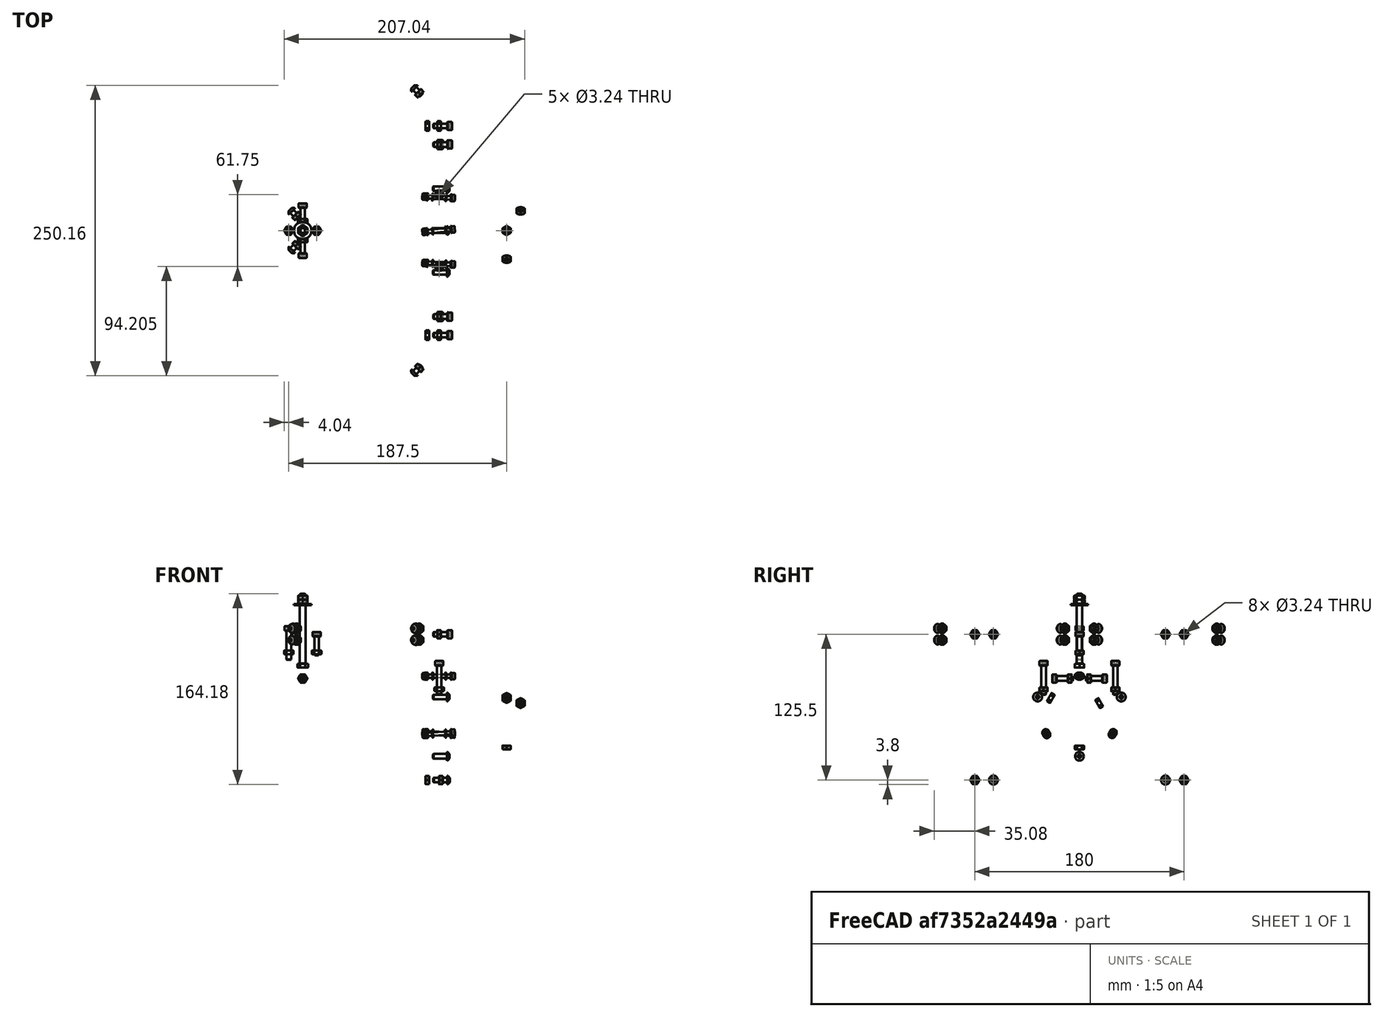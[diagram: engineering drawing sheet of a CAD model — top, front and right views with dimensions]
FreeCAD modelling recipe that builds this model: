
FCSTD DOCUMENT  (FreeCAD 0.19R24276 (Git))
Label: v5.6_Secondary
License: All rights reserved
LicenseURL: http://en.wikipedia.org/wiki/All_rights_reserved
objects: Part::FeaturePython×70, App::Link×28, App::DocumentObjectGroup×2, PartDesign::CoordinateSystem×1, App::FeaturePython×1, App::Part×1
note: 71 computed .brp shape members not serialized (recipe doc carries the construction recipe); baked Part::Feature solids carry a one-line shape summary decoded from their .brp
EXTERNAL_REF file=v5.6_Master.FCStd obj=Local_CS140
EXTERNAL_REF file=v5.6_Master.FCStd obj=Body022002
EXTERNAL_REF file=v5.6_Master.FCStd obj=Local_CS226
EXTERNAL_REF file=v5.6_Master.FCStd obj=Local_CS227
EXTERNAL_REF file=v5.6_Master.FCStd obj=Body001
EXTERNAL_REF file=v5.6_Master.FCStd obj=Local_CS003
EXTERNAL_REF file=v5.6_Master.FCStd obj=Local_CS124
EXTERNAL_REF file=v5.6_Master.FCStd obj=Body022003
EXTERNAL_REF file=v5.6_Master.FCStd obj=Local_CS062
EXTERNAL_REF file=v5.6_Master.FCStd obj=Local_CS125
EXTERNAL_REF file=v5.6_Master.FCStd obj=Body009
EXTERNAL_REF file=v5.6_Master.FCStd obj=Local_CS142
EXTERNAL_REF file=v5.6_Master.FCStd obj=Local_CS147
EXTERNAL_REF file=v5.6_Master.FCStd obj=Body011
EXTERNAL_REF file=v5.6_Master.FCStd obj=Local_CS143
EXTERNAL_REF file=v5.6_Master.FCStd obj=Local_CS146
EXTERNAL_REF file=v5.6_Master.FCStd obj=Local_CS155
EXTERNAL_REF file=v5.6_Master.FCStd obj=Local_CS181
EXTERNAL_REF file=v5.6_Master.FCStd obj=Body022005
EXTERNAL_REF file=v5.6_Master.FCStd obj=Local_CS137
EXTERNAL_REF file=v5.6_Master.FCStd obj=Local_CS201
EXTERNAL_REF file=v5.6_Master.FCStd obj=Body022004
EXTERNAL_REF file=v5.6_Master.FCStd obj=Local_CS132
EXTERNAL_REF file=v5.6_Master.FCStd obj=Local_CS134
EXTERNAL_REF file=v5.6_Master.FCStd obj=Body008
EXTERNAL_REF file=v5.6_Master.FCStd obj=Local_CS047
EXTERNAL_REF file=v5.6_Master.FCStd obj=Local_CS130
EXTERNAL_REF file=v5.6_Master.FCStd obj=Body007
EXTERNAL_REF file=v5.6_Master.FCStd obj=Local_CS046
EXTERNAL_REF file=v5.6_Master.FCStd obj=Local_CS193
EXTERNAL_REF file=v5.6_Master.FCStd obj=Body022012
EXTERNAL_REF file=v5.6_Master.FCStd obj=Local_CS036
EXTERNAL_REF file=v5.6_Master.FCStd obj=Local_CS035
EXTERNAL_REF file=v5.6_Master.FCStd obj=Local_CS045
EXTERNAL_REF file=v5.6_Master.FCStd obj=Local_CS034
EXTERNAL_REF file=v5.6_Master.FCStd obj=Local_CS033
EXTERNAL_REF file=v5.6_Master.FCStd obj=Local_CS194
EXTERNAL_REF file=v5.6_Master.FCStd obj=Local_CS123
EXTERNAL_REF file=v5.6_Master.FCStd obj=Local_CS126
EXTERNAL_REF file=v5.6_Master.FCStd obj=Local_CS127
EXTERNAL_REF file=v5.6_Master.FCStd obj=Local_CS060
EXTERNAL_REF file=v5.6_Master.FCStd obj=Local_CS136
EXTERNAL_REF file=v5.6_Master.FCStd obj=Local_CS055
EXTERNAL_REF file=v5.6_Master.FCStd obj=Local_CS191
EXTERNAL_REF file=v5.6_Master.FCStd obj=Body022010
EXTERNAL_REF file=v5.6_Master.FCStd obj=Local_CS148
EXTERNAL_REF file=v5.6_Master.FCStd obj=Local_CS150
EXTERNAL_REF file=v5.6_Master.FCStd obj=Local_CS152
EXTERNAL_REF file=v5.6_Master.FCStd obj=Local_CS149
EXTERNAL_REF file=v5.6_Master.FCStd obj=Local_CS151
EXTERNAL_REF file=v5.6_Master.FCStd obj=Local_CS153
EXTERNAL_REF file=v5.6_Master.FCStd obj=Local_CS206
EXTERNAL_REF file=v5.6_Master.FCStd obj=Local_CS205
EXTERNAL_REF file=v5.6_Master.FCStd obj=Local_CS048
EXTERNAL_REF file=v5.6_Master.FCStd obj=Local_CS049
EXTERNAL_REF file=v5.6_Master.FCStd obj=Local_CS175
EXTERNAL_REF file=v5.6_Master.FCStd obj=Body022007
EXTERNAL_REF file=v5.6_Master.FCStd obj=Local_CS157
EXTERNAL_REF file=v5.6_Master.FCStd obj=Local_CS172
EXTERNAL_REF file=v5.6_Master.FCStd obj=Body022006
EXTERNAL_REF file=v5.6_Master.FCStd obj=Local_CS156
EXTERNAL_REF file=v5.6_Master.FCStd obj=Local_CS176
EXTERNAL_REF file=v5.6_Master.FCStd obj=Local_CS177
EXTERNAL_REF file=v5.6_Master.FCStd obj=Local_CS164
EXTERNAL_REF file=v5.6_Master.FCStd obj=Local_CS168
EXTERNAL_REF file=v5.6_Master.FCStd obj=Local_CS038
EXTERNAL_REF file=v5.6_Master.FCStd obj=Local_CS037
EXTERNAL_REF file=v5.6_Master.FCStd obj=Local_CS178
EXTERNAL_REF file=v5.6_Master.FCStd obj=Local_CS179
EXTERNAL_REF file=v5.6_Master.FCStd obj=Local_CS166
EXTERNAL_REF file=v5.6_Master.FCStd obj=Local_CS043
EXTERNAL_REF file=v5.6_Master.FCStd obj=Local_CS135
EXTERNAL_REF file=v5.6_Master.FCStd obj=Local_CS141
EXTERNAL_REF file=v5.6_Master.FCStd obj=Local_CS228
EXTERNAL_REF file=v5.6_Master.FCStd obj=Body022026
EXTERNAL_REF file=v5.6_Master.FCStd obj=Local_CS224
EXTERNAL_REF file=v5.6_Master.FCStd obj=Local_CS225
EXTERNAL_REF file=v5.6_Master.FCStd obj=Local_CS229
EXTERNAL_REF file=v5.6_Master.FCStd obj=Local_CS230
EXTERNAL_REF file=v5.6_Master.FCStd obj=Body022029
EXTERNAL_REF file=v5.6_Master.FCStd obj=Local_CS231
EXTERNAL_REF file=v5.6_Master.FCStd obj=Local_CS232
EXTERNAL_REF file=v5.6_Master.FCStd obj=Local_CS238
EXTERNAL_REF file=v5.6_Master.FCStd obj=Body004
EXTERNAL_REF file=v5.6_Master.FCStd obj=Local_CS170
EXTERNAL_REF file=v5.6_Master.FCStd obj=Local_CS237
EXTERNAL_REF file=v5.6_Master.FCStd obj=Body005

FEATURE [App::DocumentObjectGroup] Parts
FEATURE [PartDesign::CoordinateSystem] LCS_Origin
  AttacherType = Attacher::AttachEngine3D
  MapMode = 2
  Support = -> [X_Axis]
FEATURE [App::DocumentObjectGroup] Constraints
FEATURE [App::FeaturePython] Variables  # WARN: FeaturePython — macro-defined, semantics opaque (R4)
FEATURE [App::Link] SecondaryMirror
  AssemblyType = Asm4EE
  AttachedBy = #Local_CS140
  AttachedTo = Parent Assembly#LCS_Origin
  LinkPlacement = pos=(-2.5,0,0) rot=(0,0,1;0rad)
  LinkedObject = -> <external v5.6_Master.FCStd>#Body022002
  Placement = pos=(-2.5,0,0) rot=(0,0,1;0rad)
  expr: Placement = LCS_Origin.Placement * AttachmentOffset * v5_6_Master#Local_CS140.Placement ^ -1
FEATURE [App::Link] SecondaryPad
  AssemblyType = Asm4EE
  AttachedBy = #Local_CS227
  AttachedTo = SecondaryOuterPad#Local_CS226
  LinkPlacement = pos=(-2.5,0,16.9706) rot=(0,0,1;0rad)
  LinkedObject = -> <external v5.6_Master.FCStd>#Body001
  Placement = pos=(-2.5,0,16.9706) rot=(0,0,1;0rad)
  expr: Placement = SecondaryOuterPad.Placement * v5_6_Master#Local_CS226.Placement * AttachmentOffset * v5_6_Master#Local_CS227.Placement ^ -1
FEATURE [App::Link] TiltPlate
  AssemblyType = Asm4EE
  AttachedBy = #Local_CS124
  AttachedTo = SecondaryPad#Local_CS003
  AttachmentOffset = pos=(0,0,0) rot=(0,0,-1;4.71239rad)
  LinkPlacement = pos=(-2.5,0,51) rot=(0,0,1;0rad)
  LinkedObject = -> <external v5.6_Master.FCStd>#Body022003
  Placement = pos=(-2.5,0,51) rot=(0,0,1;0rad)
  expr: Placement = SecondaryPad.Placement * v5_6_Master#Local_CS003.Placement * AttachmentOffset * v5_6_Master#Local_CS124.Placement ^ -1
FEATURE [App::Link] SpiderHub
  AssemblyType = Asm4EE
  AttachedBy = #Local_CS062
  AttachedTo = TiltPlate#Local_CS125
  LinkPlacement = pos=(-2.5,0,59) rot=(0,0,1;0rad)
  LinkedObject = -> <external v5.6_Master.FCStd>#Body009
  Placement = pos=(-2.5,0,59) rot=(0,0,1;0rad)
  expr: Placement = TiltPlate.Placement * v5_6_Master#Local_CS125.Placement * AttachmentOffset * v5_6_Master#Local_CS062.Placement ^ -1
FEATURE [App::Link] SpiderVane_F
  AssemblyType = Asm4EE
  AttachedBy = #Local_CS147
  AttachedTo = SpiderHub#Local_CS142
  AttachmentOffset = pos=(0,0,0) rot=(0,1,0;3.14159rad)
  LinkPlacement = pos=(-2.5,-5.3e-15,59) rot=(0,0,1;0rad)
  LinkedObject = -> <external v5.6_Master.FCStd>#Body011
  Placement = pos=(-2.5,-5.3e-15,59) rot=(0,0,1;0rad)
  expr: Placement = SpiderHub.Placement * v5_6_Master#Local_CS142.Placement * AttachmentOffset * v5_6_Master#Local_CS147.Placement ^ -1
FEATURE [App::Link] SpiderVane_A
  AssemblyType = Asm4EE
  AttachedBy = #Local_CS146
  AttachedTo = SpiderHub#Local_CS143
  AttachmentOffset = pos=(0,0,0) rot=(0,1,0;3.14159rad)
  LinkPlacement = pos=(-27.5772,25.0772,59) rot=(0,0,1;1.5708rad)
  LinkedObject = -> <external v5.6_Master.FCStd>#Body011
  Placement = pos=(-27.5772,25.0772,59) rot=(0,0,1;1.5708rad)
  expr: Placement = SpiderHub.Placement * v5_6_Master#Local_CS143.Placement * AttachmentOffset * v5_6_Master#Local_CS146.Placement ^ -1
FEATURE [App::Link] FocuserPlate
  AssemblyType = Asm4EE
  AttachedBy = #Local_CS155
  AttachedTo = SecUpperClamp_A#Local_CS181
  AttachmentOffset = pos=(0,0,0) rot=(0,0,1;3.14159rad)
  LinkPlacement = pos=(121,-1.279e-13,4.26e-14) rot=(0,0,1;0rad)
  LinkedObject = -> <external v5.6_Master.FCStd>#Body022005
  Placement = pos=(121,-1.279e-13,4.26e-14) rot=(0,0,1;0rad)
  expr: Placement = SecUpperClamp_A.Placement * v5_6_Master#Local_CS181.Placement * AttachmentOffset * v5_6_Master#Local_CS155.Placement ^ -1
FEATURE [App::Link] FocuserBase
  AssemblyType = Asm4EE
  AttachedBy = #Local_CS137
  AttachedTo = FocuserPlate#Local_CS201
  AttachmentOffset = pos=(0,0,0) rot=(0,0,1;1.5708rad)
  LinkPlacement = pos=(109,-1.157e-13,4.97e-14) rot=(0,0,1;0rad)
  LinkedObject = -> <external v5.6_Master.FCStd>#Body022004
  Placement = pos=(109,-1.157e-13,4.97e-14) rot=(0,0,1;0rad)
  expr: Placement = FocuserPlate.Placement * v5_6_Master#Local_CS201.Placement * AttachmentOffset * v5_6_Master#Local_CS137.Placement ^ -1
FEATURE [App::Link] FocuserSpring
  AssemblyType = Asm4EE
  AttachedBy = #Local_CS134
  AttachedTo = FocuserBase#Local_CS132
  LinkPlacement = pos=(109,-1.279e-13,4.62e-14) rot=(0,0,1;0rad)
  LinkedObject = -> <external v5.6_Master.FCStd>#Body008
  Placement = pos=(109,-1.279e-13,4.62e-14) rot=(0,0,1;0rad)
  expr: Placement = FocuserBase.Placement * v5_6_Master#Local_CS132.Placement * AttachmentOffset * v5_6_Master#Local_CS134.Placement ^ -1
FEATURE [App::Link] FocuserTube
  AssemblyType = Asm4EE
  AttachedBy = #Local_CS047
  AttachedTo = FocuserBase#Local_CS130
  LinkPlacement = pos=(95,-1.095e-13,5.27e-14) rot=(1,0,0;4.71239rad)
  LinkedObject = -> <external v5.6_Master.FCStd>#Body007
  Placement = pos=(95,-1.095e-13,5.27e-14) rot=(1,0,0;4.71239rad)
  expr: Placement = FocuserBase.Placement * v5_6_Master#Local_CS130.Placement * AttachmentOffset * v5_6_Master#Local_CS047.Placement ^ -1
FEATURE [App::Link] FocuserBearing_OZ
  AssemblyType = Asm4EE
  AttachedBy = #Local_CS193
  AttachedTo = FocuserSpring#Local_CS046
  AttachmentOffset = pos=(0,0,0.5) rot=(1,0,0;3.14159rad)
  LinkPlacement = pos=(122.924,0.693258,33) rot=(0.610924,-0.559809,-0.559809;2.04477rad)
  LinkedObject = -> <external v5.6_Master.FCStd>#Body022012
  Placement = pos=(122.924,0.693258,33) rot=(0.610924,-0.559809,-0.559809;2.04477rad)
  expr: Placement = FocuserSpring.Placement * v5_6_Master#Local_CS046.Placement * AttachmentOffset * v5_6_Master#Local_CS193.Placement ^ -1
FEATURE [App::Link] FocuserBearing_ONA
  AssemblyType = Asm4EE
  AttachedBy = #Local_CS193
  AttachedTo = FocuserBase#Local_CS036
  AttachmentOffset = pos=(0,0,0.5) rot=(1,0,0;3.14159rad)
  LinkPlacement = pos=(122.924,28.2322,-17.1004) rot=(0.662781,-0.193807,-0.723298;2.79007rad)
  LinkedObject = -> <external v5.6_Master.FCStd>#Body022012
  Placement = pos=(122.924,28.2322,-17.1004) rot=(0.662781,-0.193807,-0.723298;2.79007rad)
  expr: Placement = FocuserBase.Placement * v5_6_Master#Local_CS036.Placement * AttachmentOffset * v5_6_Master#Local_CS193.Placement ^ -1
FEATURE [App::Link] FocuserBearing_ONF
  AssemblyType = Asm4EE
  AttachedBy = #Local_CS193
  AttachedTo = FocuserBase#Local_CS035
  AttachmentOffset = pos=(0,0,0.5) rot=(1,0,0;3.14159rad)
  LinkPlacement = pos=(122.924,-28.9255,-15.8996) rot=(0.230763,-0.939855,-0.251834;1.71965rad)
  LinkedObject = -> <external v5.6_Master.FCStd>#Body022012
  Placement = pos=(122.924,-28.9255,-15.8996) rot=(0.230763,-0.939855,-0.251834;1.71965rad)
  expr: Placement = FocuserBase.Placement * v5_6_Master#Local_CS035.Placement * AttachmentOffset * v5_6_Master#Local_CS193.Placement ^ -1
FEATURE [App::Link] FocuserBearing_IZ
  AssemblyType = Asm4EE
  AttachedBy = #Local_CS193
  AttachedTo = FocuserSpring#Local_CS045
  AttachmentOffset = pos=(0,0,0.5) rot=(1,0,0;3.14159rad)
  LinkPlacement = pos=(107.076,-0.693258,33) rot=(-0.610924,0.559809,-0.559809;2.04477rad)
  LinkedObject = -> <external v5.6_Master.FCStd>#Body022012
  Placement = pos=(107.076,-0.693258,33) rot=(-0.610924,0.559809,-0.559809;2.04477rad)
  expr: Placement = FocuserSpring.Placement * v5_6_Master#Local_CS045.Placement * AttachmentOffset * v5_6_Master#Local_CS193.Placement ^ -1
FEATURE [App::Link] FocuserBearing_INA
  AssemblyType = Asm4EE
  AttachedBy = #Local_CS193
  AttachedTo = FocuserBase#Local_CS034
  AttachmentOffset = pos=(0,0,0.5) rot=(1,0,0;3.14159rad)
  LinkPlacement = pos=(107.076,28.9255,-15.8996) rot=(0.230763,-0.939855,0.251834;4.56353rad)
  LinkedObject = -> <external v5.6_Master.FCStd>#Body022012
  Placement = pos=(107.076,28.9255,-15.8996) rot=(0.230763,-0.939855,0.251834;4.56353rad)
  expr: Placement = FocuserBase.Placement * v5_6_Master#Local_CS034.Placement * AttachmentOffset * v5_6_Master#Local_CS193.Placement ^ -1
FEATURE [App::Link] FocuserBearing_INF
  AssemblyType = Asm4EE
  AttachedBy = #Local_CS193
  AttachedTo = FocuserBase#Local_CS033
  AttachmentOffset = pos=(0,0,0.5) rot=(1,0,0;3.14159rad)
  LinkPlacement = pos=(107.076,-28.2322,-17.1004) rot=(-0.662781,0.193807,-0.723298;2.79007rad)
  LinkedObject = -> <external v5.6_Master.FCStd>#Body022012
  Placement = pos=(107.076,-28.2322,-17.1004) rot=(-0.662781,0.193807,-0.723298;2.79007rad)
  expr: Placement = FocuserBase.Placement * v5_6_Master#Local_CS033.Placement * AttachmentOffset * v5_6_Master#Local_CS193.Placement ^ -1
FEATURE [Part::FeaturePython] Washer  label="M3-Washer"  # Fasteners workbench fastener (typed FeaturePython)
  AssemblyType = Asm4EE
  AttachedBy = Origin
  AttachedTo = FocuserBearing_OZ#Local_CS193
  Placement = pos=(120.932,0.518946,33) rot=(0.043578,-0.998099,0.043578;1.5727rad)
  diameter = 4
  invert = false
  matchOuter = false
  offset = 0
  type = 5
  expr: Placement = FocuserBearing_OZ.Placement * v5_6_Master#Local_CS193.Placement * AttachmentOffset
FEATURE [Part::FeaturePython] Washer001  label="M3-Washer591"  # Fasteners workbench fastener (typed FeaturePython)
  AssemblyType = Asm4EE
  AttachedBy = Origin
  AttachedTo = FocuserBearing_OZ#Local_CS194
  Placement = pos=(124.916,0.867569,33) rot=(0.043578,-0.998099,-0.043578;4.71049rad)
  diameter = 4
  invert = false
  matchOuter = false
  offset = 0
  type = 5
  expr: Placement = FocuserBearing_OZ.Placement * v5_6_Master#Local_CS194.Placement * AttachmentOffset
FEATURE [Part::FeaturePython] Washer002  label="M3-Washer592"  # Fasteners workbench fastener (typed FeaturePython)
  AssemblyType = Asm4EE
  AttachedBy = Origin
  AttachedTo = FocuserBearing_ONA#Local_CS193
  Placement = pos=(120.932,28.3194,-16.9494) rot=(0.419215,-0.765704,-0.487807;1.78566rad)
  diameter = 4
  invert = false
  matchOuter = false
  offset = 0
  type = 5
  expr: Placement = FocuserBearing_ONA.Placement * v5_6_Master#Local_CS193.Placement * AttachmentOffset
FEATURE [Part::FeaturePython] Washer003  label="M3-Washer593"  # Fasteners workbench fastener (typed FeaturePython)
  AssemblyType = Asm4EE
  AttachedBy = Origin
  AttachedTo = FocuserBearing_ONA#Local_CS194
  Placement = pos=(124.916,28.1451,-17.2513) rot=(-0.473306,-0.781366,-0.406753;4.41953rad)
  diameter = 4
  invert = false
  matchOuter = false
  offset = 0
  type = 5
  expr: Placement = FocuserBearing_ONA.Placement * v5_6_Master#Local_CS194.Placement * AttachmentOffset
FEATURE [Part::FeaturePython] Washer004  label="M3-Washer594"  # Fasteners workbench fastener (typed FeaturePython)
  AssemblyType = Asm4EE
  AttachedBy = Origin
  AttachedTo = FocuserBearing_ONF#Local_CS193
  Placement = pos=(120.932,-28.8383,-16.0506) rot=(-0.473306,-0.781366,0.406753;1.86366rad)
  diameter = 4
  invert = false
  matchOuter = false
  offset = 0
  type = 5
  expr: Placement = FocuserBearing_ONF.Placement * v5_6_Master#Local_CS193.Placement * AttachmentOffset
FEATURE [Part::FeaturePython] Washer005  label="M3-Washer595"  # Fasteners workbench fastener (typed FeaturePython)
  AssemblyType = Asm4EE
  AttachedBy = Origin
  AttachedTo = FocuserBearing_ONF#Local_CS194
  Placement = pos=(124.916,-29.0126,-15.7487) rot=(0.419215,-0.765704,0.487807;4.49753rad)
  diameter = 4
  invert = false
  matchOuter = false
  offset = 0
  type = 5
  expr: Placement = FocuserBearing_ONF.Placement * v5_6_Master#Local_CS194.Placement * AttachmentOffset
FEATURE [Part::FeaturePython] Washer006  label="M3-Washer596"  # Fasteners workbench fastener (typed FeaturePython)
  AssemblyType = Asm4EE
  AttachedBy = Origin
  AttachedTo = FocuserBearing_IZ#Local_CS193
  Placement = pos=(109.068,-0.518946,33) rot=(-0.043578,0.998099,0.043578;1.5727rad)
  diameter = 4
  invert = false
  matchOuter = false
  offset = 0
  type = 5
  expr: Placement = FocuserBearing_IZ.Placement * v5_6_Master#Local_CS193.Placement * AttachmentOffset
FEATURE [Part::FeaturePython] Washer007  label="M3-Washer597"  # Fasteners workbench fastener (typed FeaturePython)
  AssemblyType = Asm4EE
  AttachedBy = Origin
  AttachedTo = FocuserBearing_IZ#Local_CS194
  Placement = pos=(105.084,-0.867569,33) rot=(0.043578,-0.998099,0.043578;1.5727rad)
  diameter = 4
  invert = false
  matchOuter = false
  offset = 0
  type = 5
  expr: Placement = FocuserBearing_IZ.Placement * v5_6_Master#Local_CS194.Placement * AttachmentOffset
FEATURE [Part::FeaturePython] Washer008  label="M3-Washer598"  # Fasteners workbench fastener (typed FeaturePython)
  AssemblyType = Asm4EE
  AttachedBy = Origin
  AttachedTo = FocuserBearing_INA#Local_CS193
  Placement = pos=(109.068,28.8383,-16.0506) rot=(-0.473306,-0.781366,-0.406753;4.41953rad)
  diameter = 4
  invert = false
  matchOuter = false
  offset = 0
  type = 5
  expr: Placement = FocuserBearing_INA.Placement * v5_6_Master#Local_CS193.Placement * AttachmentOffset
FEATURE [Part::FeaturePython] Washer009  label="M3-Washer599"  # Fasteners workbench fastener (typed FeaturePython)
  AssemblyType = Asm4EE
  AttachedBy = Origin
  AttachedTo = FocuserBearing_INA#Local_CS194
  Placement = pos=(105.084,29.0126,-15.7487) rot=(-0.419215,0.765704,0.487807;4.49753rad)
  diameter = 4
  invert = false
  matchOuter = false
  offset = 0
  type = 5
  expr: Placement = FocuserBearing_INA.Placement * v5_6_Master#Local_CS194.Placement * AttachmentOffset
FEATURE [Part::FeaturePython] Washer010  label="M3-Washer600"  # Fasteners workbench fastener (typed FeaturePython)
  AssemblyType = Asm4EE
  AttachedBy = Origin
  AttachedTo = FocuserBearing_INF#Local_CS193
  Placement = pos=(109.068,-28.3194,-16.9494) rot=(-0.419215,0.765704,-0.487807;1.78566rad)
  diameter = 4
  invert = false
  matchOuter = false
  offset = 0
  type = 5
  expr: Placement = FocuserBearing_INF.Placement * v5_6_Master#Local_CS193.Placement * AttachmentOffset
FEATURE [Part::FeaturePython] Washer011  label="M3-Washer601"  # Fasteners workbench fastener (typed FeaturePython)
  AssemblyType = Asm4EE
  AttachedBy = Origin
  AttachedTo = FocuserBearing_INF#Local_CS194
  Placement = pos=(105.084,-28.1451,-17.2513) rot=(-0.473306,-0.781366,0.406753;1.86366rad)
  diameter = 4
  invert = false
  matchOuter = false
  offset = 0
  type = 5
  expr: Placement = FocuserBearing_INF.Placement * v5_6_Master#Local_CS194.Placement * AttachmentOffset
FEATURE [Part::FeaturePython] Screw  label="M5x60-Screw"  # Fasteners workbench fastener (typed FeaturePython)
  AssemblyType = Asm4EE
  AttachedBy = Origin
  AttachedTo = SecondaryPad#Local_CS123
  AttachmentOffset = pos=(0,0,0) rot=(1,0,0;3.14159rad)
  Placement = pos=(-2.5,0,43.8769) rot=(1,0,0;3.14159rad)
  diameter = 7
  invert = false
  length = 6
  lengthCustom = 60
  matchOuter = false
  offset = 0
  thread = false
  type = 26
  expr: Placement = SecondaryPad.Placement * v5_6_Master#Local_CS123.Placement * AttachmentOffset
FEATURE [Part::FeaturePython] Nut  label="M4-Nut"  # Fasteners workbench fastener (typed FeaturePython)
  AssemblyType = Asm4EE
  AttachedBy = Origin
  AttachedTo = TiltPlate#Local_CS126
  AttachmentOffset = pos=(0,0,0) rot=(-0.707107,-0.707107,0;3.14159rad)
  Placement = pos=(-14.5,6.7e-15,55) rot=(0,1,0;3.14159rad)
  diameter = 6
  invert = false
  matchOuter = false
  offset = 0
  thread = false
  type = 7
  expr: Placement = TiltPlate.Placement * v5_6_Master#Local_CS126.Placement * AttachmentOffset
FEATURE [Part::FeaturePython] Nut001  label="M4-Nut745"  # Fasteners workbench fastener (typed FeaturePython)
  AssemblyType = Asm4EE
  AttachedBy = Origin
  AttachedTo = TiltPlate#Local_CS127
  AttachmentOffset = pos=(0,0,0) rot=(0.707107,0.707107,0;3.14159rad)
  Placement = pos=(9.5,-6.7e-15,55) rot=(0,-1,0;3.14159rad)
  diameter = 6
  invert = false
  matchOuter = false
  offset = 0
  thread = false
  type = 7
  expr: Placement = TiltPlate.Placement * v5_6_Master#Local_CS127.Placement * AttachmentOffset
FEATURE [Part::FeaturePython] Screw001  label="M4x25-Screw"  # Fasteners workbench fastener (typed FeaturePython)
  AssemblyType = Asm4EE
  AttachedBy = Origin
  AttachedTo = SpiderHub#Local_CS060
  AttachmentOffset = pos=(0,0,5) rot=(0,0,1;0rad)
  Placement = pos=(-14.5,6.7e-15,72) rot=(0,0,1;0rad)
  diameter = 5
  invert = false
  length = 7
  lengthCustom = 25
  matchOuter = false
  offset = 0
  thread = false
  type = 32
  expr: Placement = SpiderHub.Placement * v5_6_Master#Local_CS060.Placement * AttachmentOffset
FEATURE [Part::FeaturePython] Screw002  label="M4x16-Screw"  # Fasteners workbench fastener (typed FeaturePython)
  AssemblyType = Asm4EE
  AttachedBy = Origin
  AttachedTo = SpiderHub#Local_CS136
  Placement = pos=(9.5,-6.7e-15,67) rot=(0,0,1;0rad)
  diameter = 5
  invert = false
  length = 5
  lengthCustom = 16
  matchOuter = false
  offset = 0
  thread = false
  type = 32
  expr: Placement = SpiderHub.Placement * v5_6_Master#Local_CS136.Placement * AttachmentOffset
FEATURE [App::Link] Sec_CollSpring
  AssemblyType = Asm4EE
  AttachedBy = #Local_CS191
  AttachedTo = SpiderHub#Local_CS055
  LinkPlacement = pos=(-2.5,0,79) rot=(0,0,-1;4.71239rad)
  LinkedObject = -> <external v5.6_Master.FCStd>#Body022010
  Placement = pos=(-2.5,0,79) rot=(0,0,-1;4.71239rad)
  expr: Placement = SpiderHub.Placement * v5_6_Master#Local_CS055.Placement * AttachmentOffset * v5_6_Master#Local_CS191.Placement ^ -1
FEATURE [Part::FeaturePython] Washer012  label="M5-Washer"  # Fasteners workbench fastener (typed FeaturePython)
  AssemblyType = Asm4EE
  AttachedBy = Origin
  AttachedTo = SpiderHub#Local_CS055
  AttachmentOffset = pos=(0,0,15) rot=(0,0,1;0rad)
  Placement = pos=(-2.5,0,94) rot=(0,0,-1;4.71239rad)
  diameter = 4
  invert = false
  matchOuter = false
  offset = 0
  type = 6
  expr: Placement = SpiderHub.Placement * v5_6_Master#Local_CS055.Placement * AttachmentOffset
FEATURE [Part::FeaturePython] Nut002  label="M5-Nut"  # Fasteners workbench fastener (typed FeaturePython)
  AssemblyType = Asm4EE
  AttachedBy = Origin
  AttachedTo = SpiderHub#Local_CS055
  AttachmentOffset = pos=(0,0,16.2) rot=(0,0,1;0rad)
  Placement = pos=(-2.5,0,95.2) rot=(0,0,-1;4.71239rad)
  diameter = 7
  invert = false
  matchOuter = false
  offset = 0
  thread = false
  type = 7
  expr: Placement = SpiderHub.Placement * v5_6_Master#Local_CS055.Placement * AttachmentOffset
FEATURE [Part::FeaturePython] Nut003  label="M5-Nut001"  # Fasteners workbench fastener (typed FeaturePython)
  AssemblyType = Asm4EE
  AttachedBy = Origin
  AttachedTo = SpiderHub#Local_CS055
  AttachmentOffset = pos=(0,0,19.8) rot=(0,0,1;0rad)
  Placement = pos=(-2.5,0,98.8) rot=(0,0,-1;4.71239rad)
  diameter = 7
  invert = false
  matchOuter = false
  offset = 0
  thread = false
  type = 7
  expr: Placement = SpiderHub.Placement * v5_6_Master#Local_CS055.Placement * AttachmentOffset
FEATURE [Part::FeaturePython] Screw003  label="M4x8-Screw"  # Fasteners workbench fastener (typed FeaturePython)
  AssemblyType = Asm4EE
  AttachedBy = Origin
  AttachedTo = SpiderVane_F#Local_CS146
  Placement = pos=(-11.7496,-16.5347,74) rot=(0.281085,0.678598,-0.678598;3.68962rad)
  diameter = 2
  invert = false
  length = 1
  lengthCustom = 8
  matchOuter = false
  offset = 0
  thread = false
  type = 38
  expr: Placement = SpiderVane_F.Placement * v5_6_Master#Local_CS146.Placement * AttachmentOffset
FEATURE [Part::FeaturePython] Screw004  label="M4x8-Screw341"  # Fasteners workbench fastener (typed FeaturePython)
  AssemblyType = Asm4EE
  AttachedBy = Origin
  AttachedTo = SpiderVane_F#Local_CS148
  Placement = pos=(-11.7496,-16.5347,64) rot=(0.281085,0.678598,-0.678598;3.68962rad)
  diameter = 2
  invert = false
  length = 1
  lengthCustom = 8
  matchOuter = false
  offset = 0
  thread = false
  type = 38
  expr: Placement = SpiderVane_F.Placement * v5_6_Master#Local_CS148.Placement * AttachmentOffset
FEATURE [Part::FeaturePython] Screw005  label="M4x8-Screw342"  # Fasteners workbench fastener (typed FeaturePython)
  AssemblyType = Asm4EE
  AttachedBy = Origin
  AttachedTo = SpiderVane_F#Local_CS150
  Placement = pos=(93.8266,-122.111,74) rot=(0.281085,0.678598,-0.678598;3.68962rad)
  diameter = 2
  invert = false
  length = 1
  lengthCustom = 8
  matchOuter = false
  offset = 0
  thread = false
  type = 38
  expr: Placement = SpiderVane_F.Placement * v5_6_Master#Local_CS150.Placement * AttachmentOffset
FEATURE [Part::FeaturePython] Screw006  label="M4x8-Screw343"  # Fasteners workbench fastener (typed FeaturePython)
  AssemblyType = Asm4EE
  AttachedBy = Origin
  AttachedTo = SpiderVane_F#Local_CS152
  Placement = pos=(93.8266,-122.111,64) rot=(0.281085,0.678598,-0.678598;3.68962rad)
  diameter = 2
  invert = false
  length = 1
  lengthCustom = 8
  matchOuter = false
  offset = 0
  thread = false
  type = 38
  expr: Placement = SpiderVane_F.Placement * v5_6_Master#Local_CS152.Placement * AttachmentOffset
FEATURE [Part::FeaturePython] Screw007  label="M4x8-Screw344"  # Fasteners workbench fastener (typed FeaturePython)
  AssemblyType = Asm4EE
  AttachedBy = Origin
  AttachedTo = SpiderVane_A#Local_CS147
  Placement = pos=(-11.7496,16.5347,74) rot=(-0.862856,-0.357407,0.357407;1.71777rad)
  diameter = 2
  invert = false
  length = 1
  lengthCustom = 8
  matchOuter = false
  offset = 0
  thread = false
  type = 38
  expr: Placement = SpiderVane_A.Placement * v5_6_Master#Local_CS147.Placement * AttachmentOffset
FEATURE [Part::FeaturePython] Screw008  label="M4x8-Screw345"  # Fasteners workbench fastener (typed FeaturePython)
  AssemblyType = Asm4EE
  AttachedBy = Origin
  AttachedTo = SpiderVane_A#Local_CS149
  Placement = pos=(-11.7496,16.5347,64) rot=(-0.862856,-0.357407,0.357407;1.71777rad)
  diameter = 2
  invert = false
  length = 1
  lengthCustom = 8
  matchOuter = false
  offset = 0
  thread = false
  type = 38
  expr: Placement = SpiderVane_A.Placement * v5_6_Master#Local_CS149.Placement * AttachmentOffset
FEATURE [Part::FeaturePython] Screw009  label="M4x8-Screw346"  # Fasteners workbench fastener (typed FeaturePython)
  AssemblyType = Asm4EE
  AttachedBy = Origin
  AttachedTo = SpiderVane_A#Local_CS151
  Placement = pos=(93.8266,122.111,74) rot=(-0.862856,-0.357407,0.357407;1.71777rad)
  diameter = 2
  invert = false
  length = 1
  lengthCustom = 8
  matchOuter = false
  offset = 0
  thread = false
  type = 38
  expr: Placement = SpiderVane_A.Placement * v5_6_Master#Local_CS151.Placement * AttachmentOffset
FEATURE [Part::FeaturePython] Screw010  label="M4x8-Screw347"  # Fasteners workbench fastener (typed FeaturePython)
  AssemblyType = Asm4EE
  AttachedBy = Origin
  AttachedTo = SpiderVane_A#Local_CS153
  Placement = pos=(93.8266,122.111,64) rot=(-0.862856,-0.357407,0.357407;1.71777rad)
  diameter = 2
  invert = false
  length = 1
  lengthCustom = 8
  matchOuter = false
  offset = 0
  thread = false
  type = 38
  expr: Placement = SpiderVane_A.Placement * v5_6_Master#Local_CS153.Placement * AttachmentOffset
FEATURE [Part::FeaturePython] Screw011  label="M4x12-Screw"  # Fasteners workbench fastener (typed FeaturePython)
  AssemblyType = Asm4EE
  AttachedBy = Origin
  AttachedTo = FocuserPlate#Local_CS201
  AttachmentOffset = pos=(0,0,0.7) rot=(0,0,1;0rad)
  Placement = pos=(121.7,-1.261e-13,-36) rot=(-0.57735,-0.57735,-0.57735;4.18879rad)
  diameter = 2
  invert = false
  length = 3
  lengthCustom = 12
  matchOuter = false
  offset = 0
  thread = false
  type = 38
  expr: Placement = FocuserPlate.Placement * v5_6_Master#Local_CS201.Placement * AttachmentOffset
FEATURE [Part::FeaturePython] Screw012  label="M4x12-Screw385"  # Fasteners workbench fastener (typed FeaturePython)
  AssemblyType = Asm4EE
  AttachedBy = Origin
  AttachedTo = FocuserPlate#Local_CS206
  AttachmentOffset = pos=(0,0,0.7) rot=(0,0,1;0rad)
  Placement = pos=(121.7,36,15) rot=(-0.57735,-0.57735,-0.57735;4.18879rad)
  diameter = 2
  invert = false
  length = 3
  lengthCustom = 12
  matchOuter = false
  offset = 0
  thread = false
  type = 38
  expr: Placement = FocuserPlate.Placement * v5_6_Master#Local_CS206.Placement * AttachmentOffset
FEATURE [Part::FeaturePython] Screw013  label="M4x12-Screw386"  # Fasteners workbench fastener (typed FeaturePython)
  AssemblyType = Asm4EE
  AttachedBy = Origin
  AttachedTo = FocuserPlate#Local_CS205
  AttachmentOffset = pos=(0,0,0.7) rot=(0,0,1;0rad)
  Placement = pos=(121.7,-36,15) rot=(-0.57735,-0.57735,-0.57735;4.18879rad)
  diameter = 2
  invert = false
  length = 3
  lengthCustom = 12
  matchOuter = false
  offset = 0
  thread = false
  type = 38
  expr: Placement = FocuserPlate.Placement * v5_6_Master#Local_CS205.Placement * AttachmentOffset
FEATURE [Part::FeaturePython] Screw014  label="M3x25-Screw"  # Fasteners workbench fastener (typed FeaturePython)
  AssemblyType = Asm4EE
  AttachedBy = Origin
  AttachedTo = FocuserBearing_OZ#Local_CS194
  AttachmentOffset = pos=(0,0,0.5) rot=(0,0,1;0rad)
  Placement = pos=(125.414,0.911147,33) rot=(0.043578,-0.998099,-0.043578;4.71049rad)
  diameter = 4
  invert = false
  length = 8
  lengthCustom = 25
  matchOuter = false
  offset = 0
  thread = false
  type = 32
  expr: Placement = FocuserBearing_OZ.Placement * v5_6_Master#Local_CS194.Placement * AttachmentOffset
FEATURE [Part::FeaturePython] Screw015  label="M3x25-Screw107"  # Fasteners workbench fastener (typed FeaturePython)
  AssemblyType = Asm4EE
  AttachedBy = Origin
  AttachedTo = FocuserBearing_ONA#Local_CS194
  AttachmentOffset = pos=(0,0,0.5) rot=(0,0,1;0rad)
  Placement = pos=(125.414,28.1233,-17.2891) rot=(-0.473306,-0.781366,-0.406753;4.41953rad)
  diameter = 4
  invert = false
  length = 8
  lengthCustom = 25
  matchOuter = false
  offset = 0
  thread = false
  type = 32
  expr: Placement = FocuserBearing_ONA.Placement * v5_6_Master#Local_CS194.Placement * AttachmentOffset
FEATURE [Part::FeaturePython] Screw016  label="M3x25-Screw108"  # Fasteners workbench fastener (typed FeaturePython)
  AssemblyType = Asm4EE
  AttachedBy = Origin
  AttachedTo = FocuserBearing_ONF#Local_CS194
  AttachmentOffset = pos=(0,0,0.5) rot=(0,0,1;0rad)
  Placement = pos=(125.414,-29.0344,-15.7109) rot=(0.419215,-0.765704,0.487807;4.49753rad)
  diameter = 4
  invert = false
  length = 8
  lengthCustom = 25
  matchOuter = false
  offset = 0
  thread = false
  type = 32
  expr: Placement = FocuserBearing_ONF.Placement * v5_6_Master#Local_CS194.Placement * AttachmentOffset
FEATURE [Part::FeaturePython] Nut004  label="M3-Nut"  # Fasteners workbench fastener (typed FeaturePython)
  AssemblyType = Asm4EE
  AttachedBy = Origin
  AttachedTo = FocuserBearing_IZ#Local_CS194
  AttachmentOffset = pos=(0,0,0.5) rot=(0,0,1;0rad)
  Placement = pos=(104.586,-0.911147,33) rot=(0.043578,-0.998099,0.043578;1.5727rad)
  diameter = 1
  invert = false
  matchOuter = false
  offset = 0
  thread = false
  type = 5
  expr: Placement = FocuserBearing_IZ.Placement * v5_6_Master#Local_CS194.Placement * AttachmentOffset
FEATURE [Part::FeaturePython] Nut005  label="M3-Nut107"  # Fasteners workbench fastener (typed FeaturePython)
  AssemblyType = Asm4EE
  AttachedBy = Origin
  AttachedTo = FocuserBearing_INA#Local_CS194
  AttachmentOffset = pos=(0,0,0.5) rot=(0,0,1;0rad)
  Placement = pos=(104.586,29.0344,-15.7109) rot=(-0.419215,0.765704,0.487807;4.49753rad)
  diameter = 1
  invert = false
  matchOuter = false
  offset = 0
  thread = false
  type = 5
  expr: Placement = FocuserBearing_INA.Placement * v5_6_Master#Local_CS194.Placement * AttachmentOffset
FEATURE [Part::FeaturePython] Nut006  label="M3-Nut108"  # Fasteners workbench fastener (typed FeaturePython)
  AssemblyType = Asm4EE
  AttachedBy = Origin
  AttachedTo = FocuserBearing_INF#Local_CS194
  AttachmentOffset = pos=(0,0,0.5) rot=(0,0,1;0rad)
  Placement = pos=(104.586,-28.1233,-17.2891) rot=(-0.473306,-0.781366,0.406753;1.86366rad)
  diameter = 1
  invert = false
  matchOuter = false
  offset = 0
  thread = false
  type = 5
  expr: Placement = FocuserBearing_INF.Placement * v5_6_Master#Local_CS194.Placement * AttachmentOffset
FEATURE [Part::FeaturePython] Nut013  label="M4-Nut746"  # Fasteners workbench fastener (typed FeaturePython)
  AssemblyType = Asm4EE
  AttachedBy = Origin
  AttachedTo = FocuserTube#Local_CS048
  Placement = pos=(173,-1.462e-13,-30) rot=(0,0,-1;4.71239rad)
  diameter = 6
  invert = false
  matchOuter = false
  offset = 0
  thread = false
  type = 7
  expr: Placement = FocuserTube.Placement * v5_6_Master#Local_CS048.Placement * AttachmentOffset
FEATURE [Part::FeaturePython] Nut014  label="M4-Nut747"  # Fasteners workbench fastener (typed FeaturePython)
  AssemblyType = Asm4EE
  AttachedBy = Origin
  AttachedTo = FocuserTube#Local_CS049
  Placement = pos=(173,-25.9808,15) rot=(0.654654,-0.654654,-0.377964;3.86433rad)
  diameter = 6
  invert = false
  matchOuter = false
  offset = 0
  thread = false
  type = 7
  expr: Placement = FocuserTube.Placement * v5_6_Master#Local_CS049.Placement * AttachmentOffset
FEATURE [App::Link] SecUpperClamp_A
  AssemblyType = Asm4EE
  AttachedBy = #Local_CS175
  AttachedTo = SpiderVane_A#Local_CS150
  AttachmentOffset = pos=(0,0,0) rot=(0,1,0;3.14159rad)
  LinkPlacement = pos=(-2.5,-9.95e-14,59) rot=(0,0,1;0rad)
  LinkedObject = -> <external v5.6_Master.FCStd>#Body022007
  Placement = pos=(-2.5,-9.95e-14,59) rot=(0,0,1;0rad)
  expr: Placement = SpiderVane_A.Placement * v5_6_Master#Local_CS150.Placement * AttachmentOffset * v5_6_Master#Local_CS175.Placement ^ -1
FEATURE [App::Link] SecUpperClamp_F
  AssemblyType = Asm4EE
  AttachedBy = #Local_CS175
  AttachedTo = SpiderVane_F#Local_CS153
  AttachmentOffset = pos=(0,0,0) rot=(1,0,0;3.14159rad)
  LinkPlacement = pos=(-2.5,9.95e-14,79) rot=(1,0,0;3.14159rad)
  LinkedObject = -> <external v5.6_Master.FCStd>#Body022007
  Placement = pos=(-2.5,9.95e-14,79) rot=(1,0,0;3.14159rad)
  expr: Placement = SpiderVane_F.Placement * v5_6_Master#Local_CS153.Placement * AttachmentOffset * v5_6_Master#Local_CS175.Placement ^ -1
FEATURE [App::Link] SecLowerClamp_A
  AssemblyType = Asm4EE
  AttachedBy = #Local_CS172
  AttachedTo = FocuserPlate#Local_CS157
  AttachmentOffset = pos=(0,0,0) rot=(0,1,0;3.14159rad)
  LinkPlacement = pos=(-2.5,-1.279e-13,-64) rot=(0,0,1;0rad)
  LinkedObject = -> <external v5.6_Master.FCStd>#Body022006
  Placement = pos=(-2.5,-1.279e-13,-64) rot=(0,0,1;0rad)
  expr: Placement = FocuserPlate.Placement * v5_6_Master#Local_CS157.Placement * AttachmentOffset * v5_6_Master#Local_CS172.Placement ^ -1
FEATURE [App::Link] SecLowerClamp_F
  AssemblyType = Asm4EE
  AttachedBy = #Local_CS172
  AttachedTo = FocuserPlate#Local_CS156
  AttachmentOffset = pos=(0,0,0) rot=(1,0,0;3.14159rad)
  LinkPlacement = pos=(-2.5,-2.84e-14,-49) rot=(-1,0,0;3.14159rad)
  LinkedObject = -> <external v5.6_Master.FCStd>#Body022006
  Placement = pos=(-2.5,-2.84e-14,-49) rot=(-1,0,0;3.14159rad)
  expr: Placement = FocuserPlate.Placement * v5_6_Master#Local_CS156.Placement * AttachmentOffset * v5_6_Master#Local_CS172.Placement ^ -1
FEATURE [Part::FeaturePython] Nut015  label="M4-Nut748"  # Fasteners workbench fastener (typed FeaturePython)
  AssemblyType = Asm4EE
  AttachedBy = Origin
  AttachedTo = SecUpperClamp_A#Local_CS176
  AttachmentOffset = pos=(0,0,0) rot=(0,1,0;3.14159rad)
  Placement = pos=(116.5,74,69) rot=(-0.57735,-0.57735,0.57735;2.0944rad)
  diameter = 6
  invert = false
  matchOuter = false
  offset = 0
  thread = false
  type = 7
  expr: Placement = SecUpperClamp_A.Placement * v5_6_Master#Local_CS176.Placement * AttachmentOffset
FEATURE [Part::FeaturePython] Nut016  label="M4-Nut749"  # Fasteners workbench fastener (typed FeaturePython)
  AssemblyType = Asm4EE
  AttachedBy = Origin
  AttachedTo = SecUpperClamp_A#Local_CS177
  AttachmentOffset = pos=(0,0,0) rot=(0,1,0;3.14159rad)
  Placement = pos=(116.5,90,69) rot=(-0.57735,-0.57735,0.57735;2.0944rad)
  diameter = 6
  invert = false
  matchOuter = false
  offset = 0
  thread = false
  type = 7
  expr: Placement = SecUpperClamp_A.Placement * v5_6_Master#Local_CS177.Placement * AttachmentOffset
FEATURE [Part::FeaturePython] Nut017  label="M4-Nut750"  # Fasteners workbench fastener (typed FeaturePython)
  AssemblyType = Asm4EE
  AttachedBy = Origin
  AttachedTo = SecUpperClamp_F#Local_CS176
  AttachmentOffset = pos=(0,0,0) rot=(0,1,0;3.14159rad)
  Placement = pos=(116.5,-74,69) rot=(-0.57735,0.57735,0.57735;4.18879rad)
  diameter = 6
  invert = false
  matchOuter = false
  offset = 0
  thread = false
  type = 7
  expr: Placement = SecUpperClamp_F.Placement * v5_6_Master#Local_CS176.Placement * AttachmentOffset
FEATURE [Part::FeaturePython] Nut018  label="M4-Nut751"  # Fasteners workbench fastener (typed FeaturePython)
  AssemblyType = Asm4EE
  AttachedBy = Origin
  AttachedTo = SecUpperClamp_F#Local_CS177
  AttachmentOffset = pos=(0,0,0) rot=(0,-1,0;3.14159rad)
  Placement = pos=(116.5,-90,69) rot=(0.57735,-0.57735,-0.57735;2.0944rad)
  diameter = 6
  invert = false
  matchOuter = false
  offset = 0
  thread = false
  type = 7
  expr: Placement = SecUpperClamp_F.Placement * v5_6_Master#Local_CS177.Placement * AttachmentOffset
FEATURE [Part::FeaturePython] Nut019  label="M4-Nut752"  # Fasteners workbench fastener (typed FeaturePython)
  AssemblyType = Asm4EE
  AttachedBy = Origin
  AttachedTo = SecLowerClamp_A#Local_CS164
  Placement = pos=(118,74,-56.5) rot=(0.57735,-0.57735,-0.57735;2.0944rad)
  diameter = 6
  invert = false
  matchOuter = false
  offset = 0
  thread = false
  type = 7
  expr: Placement = SecLowerClamp_A.Placement * v5_6_Master#Local_CS164.Placement * AttachmentOffset
FEATURE [Part::FeaturePython] Nut020  label="M4-Nut753"  # Fasteners workbench fastener (typed FeaturePython)
  AssemblyType = Asm4EE
  AttachedBy = Origin
  AttachedTo = SecLowerClamp_A#Local_CS168
  Placement = pos=(106.5,90,-56.5) rot=(0.57735,-0.57735,-0.57735;2.0944rad)
  diameter = 6
  invert = false
  matchOuter = false
  offset = 0
  thread = false
  type = 7
  expr: Placement = SecLowerClamp_A.Placement * v5_6_Master#Local_CS168.Placement * AttachmentOffset
FEATURE [Part::FeaturePython] Nut021  label="M4-Nut754"  # Fasteners workbench fastener (typed FeaturePython)
  AssemblyType = Asm4EE
  AttachedBy = Origin
  AttachedTo = SecLowerClamp_F#Local_CS164
  Placement = pos=(118,-74,-56.5) rot=(-0.57735,-0.57735,0.57735;2.0944rad)
  diameter = 6
  invert = false
  matchOuter = false
  offset = 0
  thread = false
  type = 7
  expr: Placement = SecLowerClamp_F.Placement * v5_6_Master#Local_CS164.Placement * AttachmentOffset
FEATURE [Part::FeaturePython] Nut022  label="M4-Nut755"  # Fasteners workbench fastener (typed FeaturePython)
  AssemblyType = Asm4EE
  AttachedBy = Origin
  AttachedTo = SecLowerClamp_F#Local_CS168
  Placement = pos=(106.5,-90,-56.5) rot=(-0.57735,-0.57735,0.57735;2.0944rad)
  diameter = 6
  invert = false
  matchOuter = false
  offset = 0
  thread = false
  type = 7
  expr: Placement = SecLowerClamp_F.Placement * v5_6_Master#Local_CS168.Placement * AttachmentOffset
FEATURE [Part::FeaturePython] Nut023  label="M4-Nut756"  # Fasteners workbench fastener (typed FeaturePython)
  AssemblyType = Asm4EE
  AttachedBy = Origin
  AttachedTo = FocuserBase#Local_CS038
  AttachmentOffset = pos=(0,0,0) rot=(0.707107,-0.707107,0;3.14159rad)
  Placement = pos=(115,30.875,23.25) rot=(-1,0,0;3.14159rad)
  diameter = 6
  invert = false
  matchOuter = false
  offset = 0
  thread = false
  type = 7
  expr: Placement = FocuserBase.Placement * v5_6_Master#Local_CS038.Placement * AttachmentOffset
FEATURE [Part::FeaturePython] Nut024  label="M4-Nut757"  # Fasteners workbench fastener (typed FeaturePython)
  AssemblyType = Asm4EE
  AttachedBy = Origin
  AttachedTo = FocuserBase#Local_CS037
  AttachmentOffset = pos=(0,0,0) rot=(0.707107,-0.707107,0;3.14159rad)
  Placement = pos=(115,-30.875,23.25) rot=(-1,0,0;3.14159rad)
  diameter = 6
  invert = false
  matchOuter = false
  offset = 0
  thread = false
  type = 7
  expr: Placement = FocuserBase.Placement * v5_6_Master#Local_CS037.Placement * AttachmentOffset
FEATURE [Part::FeaturePython] Screw025  label="M4x12-Screw387"  # Fasteners workbench fastener (typed FeaturePython)
  AssemblyType = Asm4EE
  AttachedBy = Origin
  AttachedTo = SecUpperClamp_A#Local_CS178
  Placement = pos=(122,74,69) rot=(0.57735,-0.57735,0.57735;4.18879rad)
  diameter = 5
  invert = false
  length = 3
  lengthCustom = 12
  matchOuter = false
  offset = 0
  thread = false
  type = 32
  expr: Placement = SecUpperClamp_A.Placement * v5_6_Master#Local_CS178.Placement * AttachmentOffset
FEATURE [Part::FeaturePython] Screw026  label="M4x12-Screw388"  # Fasteners workbench fastener (typed FeaturePython)
  AssemblyType = Asm4EE
  AttachedBy = Origin
  AttachedTo = SecUpperClamp_A#Local_CS179
  Placement = pos=(122,90,69) rot=(0.57735,-0.57735,0.57735;4.18879rad)
  diameter = 5
  invert = false
  length = 3
  lengthCustom = 12
  matchOuter = false
  offset = 0
  thread = false
  type = 32
  expr: Placement = SecUpperClamp_A.Placement * v5_6_Master#Local_CS179.Placement * AttachmentOffset
FEATURE [Part::FeaturePython] Screw027  label="M4x12-Screw389"  # Fasteners workbench fastener (typed FeaturePython)
  AssemblyType = Asm4EE
  AttachedBy = Origin
  AttachedTo = SecUpperClamp_F#Local_CS178
  Placement = pos=(122,-74,69) rot=(0.57735,0.57735,0.57735;2.0944rad)
  diameter = 5
  invert = false
  length = 3
  lengthCustom = 12
  matchOuter = false
  offset = 0
  thread = false
  type = 32
  expr: Placement = SecUpperClamp_F.Placement * v5_6_Master#Local_CS178.Placement * AttachmentOffset
FEATURE [Part::FeaturePython] Screw028  label="M4x12-Screw390"  # Fasteners workbench fastener (typed FeaturePython)
  AssemblyType = Asm4EE
  AttachedBy = Origin
  AttachedTo = SecUpperClamp_F#Local_CS179
  Placement = pos=(122,-90,69) rot=(0.57735,0.57735,0.57735;2.0944rad)
  diameter = 5
  invert = false
  length = 3
  lengthCustom = 12
  matchOuter = false
  offset = 0
  thread = false
  type = 32
  expr: Placement = SecUpperClamp_F.Placement * v5_6_Master#Local_CS179.Placement * AttachmentOffset
FEATURE [Part::FeaturePython] Screw029  label="M4x12-Screw391"  # Fasteners workbench fastener (typed FeaturePython)
  AssemblyType = Asm4EE
  AttachedBy = Origin
  AttachedTo = SecLowerClamp_A#Local_CS166
  Placement = pos=(122,74,-56.5) rot=(0.57735,0.57735,0.57735;2.0944rad)
  diameter = 2
  invert = false
  length = 3
  lengthCustom = 12
  matchOuter = false
  offset = 0
  thread = false
  type = 38
  expr: Placement = SecLowerClamp_A.Placement * v5_6_Master#Local_CS166.Placement * AttachmentOffset
FEATURE [Part::FeaturePython] Screw030  label="M4x12-Screw392"  # Fasteners workbench fastener (typed FeaturePython)
  AssemblyType = Asm4EE
  AttachedBy = Origin
  AttachedTo = SecLowerClamp_F#Local_CS166
  Placement = pos=(122,-74,-56.5) rot=(-0.57735,0.57735,-0.57735;2.0944rad)
  diameter = 2
  invert = false
  length = 3
  lengthCustom = 12
  matchOuter = false
  offset = 0
  thread = false
  type = 38
  expr: Placement = SecLowerClamp_F.Placement * v5_6_Master#Local_CS166.Placement * AttachmentOffset
FEATURE [Part::FeaturePython] Screw033  label="M4x25-Screw111"  # Fasteners workbench fastener (typed FeaturePython)
  AssemblyType = Asm4EE
  AttachedBy = Origin
  AttachedTo = FocuserSpring#Local_CS043
  Placement = pos=(115,30.875,42) rot=(0,0,-1;4.71239rad)
  diameter = 5
  invert = false
  length = 7
  lengthCustom = 25
  matchOuter = false
  offset = 0
  thread = false
  type = 32
  expr: Placement = FocuserSpring.Placement * v5_6_Master#Local_CS043.Placement * AttachmentOffset
FEATURE [Part::FeaturePython] Screw034  label="M4x25-Screw112"  # Fasteners workbench fastener (typed FeaturePython)
  AssemblyType = Asm4EE
  AttachedBy = Origin
  AttachedTo = FocuserSpring#Local_CS135
  Placement = pos=(115,-30.875,42) rot=(0,0,-1;4.71239rad)
  diameter = 5
  invert = false
  length = 7
  lengthCustom = 25
  matchOuter = false
  offset = 0
  thread = false
  type = 32
  expr: Placement = FocuserSpring.Placement * v5_6_Master#Local_CS135.Placement * AttachmentOffset
FEATURE [App::Link] SecondaryOuterPad
  AssemblyType = Asm4EE
  AttachedBy = #Local_CS228
  AttachedTo = SecondaryMirror#Local_CS141
  LinkPlacement = pos=(-2.5,0,16.9706) rot=(0,0,1;0rad)
  LinkedObject = -> <external v5.6_Master.FCStd>#Body022026
  Placement = pos=(-2.5,0,16.9706) rot=(0,0,1;0rad)
  expr: Placement = SecondaryMirror.Placement * v5_6_Master#Local_CS141.Placement * AttachmentOffset * v5_6_Master#Local_CS228.Placement ^ -1
FEATURE [Part::FeaturePython] Nut025  label="M4-Nut758"  # Fasteners workbench fastener (typed FeaturePython)
  AssemblyType = Asm4EE
  AttachedBy = Origin
  AttachedTo = SecondaryPad#Local_CS224
  AttachmentOffset = pos=(0,0,0) rot=(0,0,1;1.5708rad)
  Placement = pos=(-2.5,-10,30.9706) rot=(0,0.707107,0.707107;3.14159rad)
  diameter = 6
  invert = false
  matchOuter = false
  offset = 0
  thread = false
  type = 7
  expr: Placement = SecondaryPad.Placement * v5_6_Master#Local_CS224.Placement * AttachmentOffset
FEATURE [Part::FeaturePython] Nut026  label="M4-Nut759"  # Fasteners workbench fastener (typed FeaturePython)
  AssemblyType = Asm4EE
  AttachedBy = Origin
  AttachedTo = SecondaryPad#Local_CS225
  AttachmentOffset = pos=(0,0,0) rot=(0,0,1;1.5708rad)
  Placement = pos=(-2.5,10,30.9706) rot=(0,-0.707107,0.707107;3.14159rad)
  diameter = 6
  invert = false
  matchOuter = false
  offset = 0
  thread = false
  type = 7
  expr: Placement = SecondaryPad.Placement * v5_6_Master#Local_CS225.Placement * AttachmentOffset
FEATURE [Part::FeaturePython] Screw035  label="M4x14-Screw"  # Fasteners workbench fastener (typed FeaturePython)
  AssemblyType = Asm4EE
  AttachedBy = Origin
  AttachedTo = SecondaryPad#Local_CS224
  AttachmentOffset = pos=(0,0,-9.5) rot=(1,0,0;3.14159rad)
  Placement = pos=(-2.5,-19.5,30.9706) rot=(0.57735,0.57735,-0.57735;2.0944rad)
  diameter = 5
  invert = false
  length = 4
  lengthCustom = 14
  matchOuter = false
  offset = 0
  thread = false
  type = 32
  expr: Placement = SecondaryPad.Placement * v5_6_Master#Local_CS224.Placement * AttachmentOffset
FEATURE [Part::FeaturePython] Screw036  label="M4x14-Screw001"  # Fasteners workbench fastener (typed FeaturePython)
  AssemblyType = Asm4EE
  AttachedBy = Origin
  AttachedTo = SecondaryPad#Local_CS225
  AttachmentOffset = pos=(0,0,-9.5) rot=(1,0,0;3.14159rad)
  Placement = pos=(-2.5,19.5,30.9706) rot=(0.57735,0.57735,0.57735;4.18879rad)
  diameter = 5
  invert = false
  length = 4
  lengthCustom = 14
  matchOuter = false
  offset = 0
  thread = false
  type = 32
  expr: Placement = SecondaryPad.Placement * v5_6_Master#Local_CS225.Placement * AttachmentOffset
FEATURE [App::Link] EyepieceAdaptor
  AssemblyType = Asm4EE
  AttachedBy = #Local_CS230
  AttachedTo = FocuserTube#Local_CS229
  AttachmentOffset = pos=(0,0,0) rot=(0,0,1;1.5708rad)
  LinkPlacement = pos=(179,-1.454e-13,3.59e-14) rot=(-1,0,0;1.5708rad)
  LinkedObject = -> <external v5.6_Master.FCStd>#Body022029
  Placement = pos=(179,-1.454e-13,3.59e-14) rot=(-1,0,0;1.5708rad)
  expr: Placement = FocuserTube.Placement * v5_6_Master#Local_CS229.Placement * AttachmentOffset * v5_6_Master#Local_CS230.Placement ^ -1
FEATURE [Part::FeaturePython] Nut027  label="M4-Nut760"  # Fasteners workbench fastener (typed FeaturePython)
  AssemblyType = Asm4EE
  AttachedBy = Origin
  AttachedTo = EyepieceAdaptor#Local_CS231
  Placement = pos=(185,18.3164,10.575) rot=(0.654654,-0.654654,0.377964;2.41886rad)
  diameter = 6
  invert = false
  matchOuter = false
  offset = 0
  thread = false
  type = 7
  expr: Placement = EyepieceAdaptor.Placement * v5_6_Master#Local_CS231.Placement * AttachmentOffset
FEATURE [Part::FeaturePython] Nut028  label="M4-Nut761"  # Fasteners workbench fastener (typed FeaturePython)
  AssemblyType = Asm4EE
  AttachedBy = Origin
  AttachedTo = SpiderVane_F#Local_CS147
  AttachmentOffset = pos=(0,0,3) rot=(0,0,1;1.5708rad)
  Placement = pos=(-8.92115,-13.7063,74) rot=(-0.357407,0.862856,0.357407;1.71777rad)
  diameter = 6
  invert = false
  matchOuter = false
  offset = 0
  thread = false
  type = 7
  expr: Placement = SpiderVane_F.Placement * v5_6_Master#Local_CS147.Placement * AttachmentOffset
FEATURE [Part::FeaturePython] Nut029  label="M4-Nut762"  # Fasteners workbench fastener (typed FeaturePython)
  AssemblyType = Asm4EE
  AttachedBy = Origin
  AttachedTo = SpiderVane_F#Local_CS149
  AttachmentOffset = pos=(0,0,3) rot=(0,0,1;1.5708rad)
  Placement = pos=(-8.92115,-13.7063,64) rot=(-0.357407,0.862856,0.357407;1.71777rad)
  diameter = 6
  invert = false
  matchOuter = false
  offset = 0
  thread = false
  type = 7
  expr: Placement = SpiderVane_F.Placement * v5_6_Master#Local_CS149.Placement * AttachmentOffset
FEATURE [Part::FeaturePython] Nut030  label="M4-Nut763"  # Fasteners workbench fastener (typed FeaturePython)
  AssemblyType = Asm4EE
  AttachedBy = Origin
  AttachedTo = SpiderVane_A#Local_CS146
  AttachmentOffset = pos=(0,0,3) rot=(0,0,1;1.5708rad)
  Placement = pos=(-8.92115,13.7063,74) rot=(0.357407,0.862856,-0.357407;1.71777rad)
  diameter = 6
  invert = false
  matchOuter = false
  offset = 0
  thread = false
  type = 7
  expr: Placement = SpiderVane_A.Placement * v5_6_Master#Local_CS146.Placement * AttachmentOffset
FEATURE [Part::FeaturePython] Nut031  label="M4-Nut764"  # Fasteners workbench fastener (typed FeaturePython)
  AssemblyType = Asm4EE
  AttachedBy = Origin
  AttachedTo = SpiderVane_A#Local_CS148
  AttachmentOffset = pos=(0,0,3) rot=(0,0,1;1.5708rad)
  Placement = pos=(-8.92115,13.7063,64) rot=(0.357407,0.862856,-0.357407;1.71777rad)
  diameter = 6
  invert = false
  matchOuter = false
  offset = 0
  thread = false
  type = 7
  expr: Placement = SpiderVane_A.Placement * v5_6_Master#Local_CS148.Placement * AttachmentOffset
FEATURE [Part::FeaturePython] Nut032  label="M4-Nut765"  # Fasteners workbench fastener (typed FeaturePython)
  AssemblyType = Asm4EE
  AttachedBy = Origin
  AttachedTo = SpiderVane_F#Local_CS151
  AttachmentOffset = pos=(0,0,3) rot=(0,0,1;1.5708rad)
  Placement = pos=(96.6551,-119.282,74) rot=(-0.357407,0.862856,0.357407;1.71777rad)
  diameter = 6
  invert = false
  matchOuter = false
  offset = 0
  thread = false
  type = 7
  expr: Placement = SpiderVane_F.Placement * v5_6_Master#Local_CS151.Placement * AttachmentOffset
FEATURE [Part::FeaturePython] Nut033  label="M4-Nut766"  # Fasteners workbench fastener (typed FeaturePython)
  AssemblyType = Asm4EE
  AttachedBy = Origin
  AttachedTo = SpiderVane_F#Local_CS153
  AttachmentOffset = pos=(0,0,3) rot=(0,0,1;1.5708rad)
  Placement = pos=(96.6551,-119.282,64) rot=(-0.357407,0.862856,0.357407;1.71777rad)
  diameter = 6
  invert = false
  matchOuter = false
  offset = 0
  thread = false
  type = 7
  expr: Placement = SpiderVane_F.Placement * v5_6_Master#Local_CS153.Placement * AttachmentOffset
FEATURE [Part::FeaturePython] Nut034  label="M4-Nut767"  # Fasteners workbench fastener (typed FeaturePython)
  AssemblyType = Asm4EE
  AttachedBy = Origin
  AttachedTo = SpiderVane_A#Local_CS150
  AttachmentOffset = pos=(0,0,3) rot=(0,0,1;1.5708rad)
  Placement = pos=(96.6551,119.282,74) rot=(0.357407,0.862856,-0.357407;1.71777rad)
  diameter = 6
  invert = false
  matchOuter = false
  offset = 0
  thread = false
  type = 7
  expr: Placement = SpiderVane_A.Placement * v5_6_Master#Local_CS150.Placement * AttachmentOffset
FEATURE [Part::FeaturePython] Nut035  label="M4-Nut768"  # Fasteners workbench fastener (typed FeaturePython)
  AssemblyType = Asm4EE
  AttachedBy = Origin
  AttachedTo = SpiderVane_A#Local_CS152
  AttachmentOffset = pos=(0,0,3) rot=(0,0,1;1.5708rad)
  Placement = pos=(96.6551,119.282,64) rot=(0.357407,0.862856,-0.357407;1.71777rad)
  diameter = 6
  invert = false
  matchOuter = false
  offset = 0
  thread = false
  type = 7
  expr: Placement = SpiderVane_A.Placement * v5_6_Master#Local_CS152.Placement * AttachmentOffset
FEATURE [App::Link] EyepieceAdaptor_Screw
  AssemblyType = Asm4EE
  AttachedBy = #Local_CS238
  AttachedTo = EyepieceAdaptor#Local_CS232
  AttachmentOffset = pos=(0,0,-1) rot=(1,0,0;3.14159rad)
  LinkPlacement = pos=(185,22.6466,13.075) rot=(0,0.5,0.866025;3.14159rad)
  LinkedObject = -> <external v5.6_Master.FCStd>#Body004
  Placement = pos=(185,22.6466,13.075) rot=(0,0.5,0.866025;3.14159rad)
  expr: Placement = EyepieceAdaptor.Placement * v5_6_Master#Local_CS232.Placement * AttachmentOffset * v5_6_Master#Local_CS238.Placement ^ -1
FEATURE [App::Link] FocuserClamp_Screw1
  AssemblyType = Asm4EE
  AttachedBy = #Local_CS238
  AttachedTo = FocuserTube#Local_CS048
  AttachmentOffset = pos=(0,0,-6) rot=(1,0,0;3.14159rad)
  LinkPlacement = pos=(173,-1.476e-13,-36) rot=(0,-1,0;3.14159rad)
  LinkedObject = -> <external v5.6_Master.FCStd>#Body004
  Placement = pos=(173,-1.476e-13,-36) rot=(0,-1,0;3.14159rad)
  expr: Placement = FocuserTube.Placement * v5_6_Master#Local_CS048.Placement * AttachmentOffset * v5_6_Master#Local_CS238.Placement ^ -1
FEATURE [App::Link] FocuserClamp_Screw2
  AssemblyType = Asm4EE
  AttachedBy = #Local_CS238
  AttachedTo = FocuserTube#Local_CS049
  AttachmentOffset = pos=(0,0,-6) rot=(1,0,0;3.14159rad)
  LinkPlacement = pos=(173,-31.1769,18) rot=(0,-0.5,0.866025;3.14159rad)
  LinkedObject = -> <external v5.6_Master.FCStd>#Body004
  Placement = pos=(173,-31.1769,18) rot=(0,-0.5,0.866025;3.14159rad)
  expr: Placement = FocuserTube.Placement * v5_6_Master#Local_CS049.Placement * AttachmentOffset * v5_6_Master#Local_CS238.Placement ^ -1
FEATURE [App::Link] LowerClamp_A_Knob
  AssemblyType = Asm4EE
  AttachedBy = #Local_CS237
  AttachedTo = SecLowerClamp_A#Local_CS170
  LinkPlacement = pos=(122,90,-56.5) rot=(0,1,0;1.5708rad)
  LinkedObject = -> <external v5.6_Master.FCStd>#Body005
  Placement = pos=(122,90,-56.5) rot=(0,1,0;1.5708rad)
  expr: Placement = SecLowerClamp_A.Placement * v5_6_Master#Local_CS170.Placement * AttachmentOffset * v5_6_Master#Local_CS237.Placement ^ -1
FEATURE [App::Link] LowerClamp_F_Knob
  AssemblyType = Asm4EE
  AttachedBy = #Local_CS237
  AttachedTo = SecLowerClamp_F#Local_CS170
  LinkPlacement = pos=(122,-90,-56.5) rot=(-0.707107,0,-0.707107;3.14159rad)
  LinkedObject = -> <external v5.6_Master.FCStd>#Body005
  Placement = pos=(122,-90,-56.5) rot=(-0.707107,0,-0.707107;3.14159rad)
  expr: Placement = SecLowerClamp_F.Placement * v5_6_Master#Local_CS170.Placement * AttachmentOffset * v5_6_Master#Local_CS237.Placement ^ -1
FEATURE [App::Part] Model  label="Secondary"
  Configuration = 0
  Group = -> [LCS_Origin,Constraints,Variables,SecondaryMirror,SecondaryPad,TiltPlate,SpiderHub,SpiderVane_F,SpiderVane_A,FocuserPlate,FocuserBase,FocuserSpring,FocuserTube,FocuserBearing_OZ,FocuserBearing_ONA,FocuserBearing_ONF,FocuserBearing_IZ,FocuserBearing_INA,FocuserBearing_INF,Washer,Washer001,Washer002,Washer003,Washer004,Washer005,Washer006,Washer007,Washer008,Washer009,Washer010,Washer011,Screw,Nut,+68 more]
  Origin = -> Origin
  Type = Assembly4 Model

RESOLVED EXTERNAL PARTS (link-assembly join: the EXTERNAL_REF files above that resolve inside this repo's crawl, each included once):
---- part v5.6_Master.FCStd = doc fcstd_204eddf974d0 (447149 chars; too large to inline — full recipe in that document) ----
